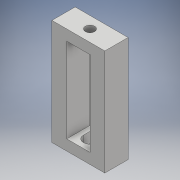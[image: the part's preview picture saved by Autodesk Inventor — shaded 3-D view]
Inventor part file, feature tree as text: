
AUTODESK INVENTOR PART (.ipt)
format: ipt  version: 2017 (Build 210142000, 142)  size: 179,200 bytes
history: native  units: mm
features: extrude x7, sketch x5, projected_geometry x1
ambient origin geometry x8: Origin, YZ Plane, XZ Plane, XY Plane, X Axis, Y Axis, Z Axis, Center Point
bodies: Solid1 (feature_tree)
feature tree (13):
  sketch  "Sketch1"  dims[d0=6.2mm d1=11.0mm]
  extrude  "Extr-legs"  Depth=11.0mm
  extrude  "Extr-base"  Depth=7.0mm
  sketch  "Sketch2"  dims[d2=7.0mm d3=7.0mm]
  extrude  "Extr-top"  Depth=5.0mm TaperAngle=0.0deg
  extrude  "Extrusion4"  Depth=9.0mm
  extrude  "Extrusion5"  Depth=10.0mm TaperAngle=0.0deg
  extrude  "Extrusion6"  Depth=10.0mm TaperAngle=0.0deg
  extrude  "Extrusion7"  Depth=10.0mm TaperAngle=0.0deg
  sketch  "Sketch3"  dims[d4=40.0mm d5=0.0mm d6=5.0mm d7=0.0mm]
  projected_geometry  "Projected Loop1"
  sketch  "Sketch4"  dims[d8=4.4mm d9=9.0mm]
  sketch  "Sketch5"  dims[d10=5.0mm d11=0.0mm d12=10.0mm d13=0.0mm d15=10.0mm d16=0.0mm d17=10.0mm d18=0.0mm d19=10.0mm d20=0.0mm]
